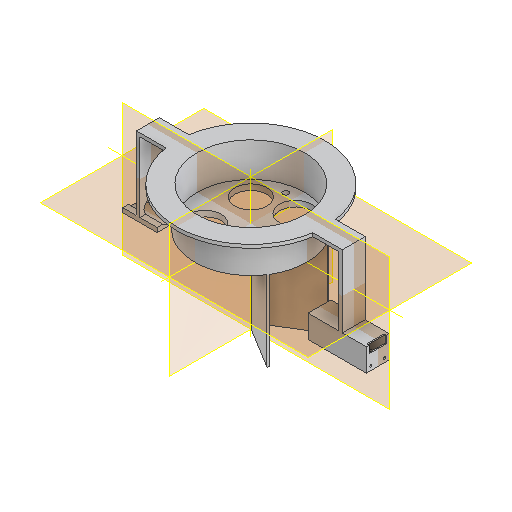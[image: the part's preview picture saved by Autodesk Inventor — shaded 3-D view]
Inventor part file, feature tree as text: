
AUTODESK INVENTOR PART (.ipt)
format: ipt  version: 2025.1 (Build 291241000, 241)  size: 340,992 bytes
history: native  units: mm
features: extrude x15, sketch x15, mirror x1
ambient origin geometry x8: Origin, YZ Plane, XZ Plane, XY Plane, X Axis, Y Axis, Z Axis, Center Point
bodies: Solid1 (feature_tree)
feature tree (31):
  extrude  "Extrusion1"  Depth=35.0mm TaperAngle=0.0deg
  extrude  "Extrusion3"  Depth=30.0mm TaperAngle=0.0deg
  extrude  "Extrusion4"  Depth=130.0mm
  extrude  "Extrusion5"  TaperAngle=0.0deg  [1 undecoded]
  extrude  "Extrusion6"  Depth=10.0mm
  mirror  "Mirror1"
  extrude  "Extrusion7"  Depth=20.0mm
  extrude  "Extrusion9"  Depth=65.0mm TaperAngle=0.0deg
  extrude  "Extrusion10"  Depth=8.0mm
  extrude  "Extrusion15"  Depth=5.0mm
  extrude  "Extrusion16"  Depth=15.0mm TaperAngle=0.0deg
  extrude  "Extrusion17"  Depth=30.0mm
  extrude  "Extrusion18"  Depth=28.0mm
  extrude  "Extrusion19"  Depth=28.0mm
  extrude  "Extrusion20"  Depth=20.0mm
  extrude  "Extrusion21"  Depth=12.0mm
  sketch  "Sketch1"  dims[d1=98.0mm d2=35.0mm d3=0.0mm]
  sketch  "Sketch4"  dims[d8=94.0mm d9=30.0mm d10=0.0mm]
  sketch  "Sketch6"  dims[d13=98.0mm d14=130.0mm]
  sketch  "Sketch7"  dims[d15=3.0mm d16=0.0mm d36=0.0mm d37=0.0mm]
  sketch  "Sketch9"  dims[d39=3.0mm d40=0.0mm d41=10.0mm]
  sketch  "Sketch10"  dims[d42=20.0mm d43=90.0mm]
  sketch  "Sketch12"  dims[d44=3.0mm d45=65.0mm d46=0.0mm]
  sketch  "Sketch13"  dims[d49=13.0mm d50=8.0mm]
  sketch  "Sketch18"  dims[d51=3.0mm d52=0.0mm d53=5.0mm]
  sketch  "Sketch19"  dims[d54=5.0mm d55=15.0mm d56=15.0mm d57=0.0mm d58=0.0mm]
  sketch  "Sketch20"  dims[d92=28.0mm d93=30.0mm]
  sketch  "Sketch21"  dims[d94=28.0mm d95=30.0mm d96=28.0mm d97=30.0mm]
  sketch  "Sketch22"  dims[d98=28.0mm d99=30.0mm d100=28.0mm d101=30.0mm d102=20.0mm]
  sketch  "Sketch23"  dims[d103=20.0mm d104=20.0mm]
  sketch  "Sketch24"  dims[d105=20.0mm d106=12.0mm d107=27.0mm d108=12.0mm d109=27.0mm d110=5.0mm d111=5.0mm d112=5.0mm d115=3.5mm d116=70.0mm d117=0.0mm d118=3.0mm d119=80.0mm d120=0.0mm d121=20.0mm d122=18.0mm d123=18.0mm d124=19.0mm d125=1.0mm d126=3.0mm d127=0.0mm d128=20.0mm d129=20.0mm d130=30.0mm d131=0.0mm d132=0.0mm d133=1.0mm d134=0.0mm d135=15.0mm d136=7.5mm d137=4.0mm d138=17.5mm d139=10.0mm d140=2.0mm d141=4.0mm d142=2.0mm d143=10.0mm d144=4.0mm d145=1.0mm d146=0.0mm d147=15.0mm d148=2.5mm d149=2.0mm d150=4.0mm d151=0.0mm d38=0.5mm d86=0.5mm d87=0.872665mm d88=0.5mm d89=0.872665mm d152=0.5mm d153=0.872665mm]
note: 1 required parameter value undecoded (feature->parameter linkage not recoverable at this tier; creation-order binding heuristic only, values carry confidence <= 0.55)
